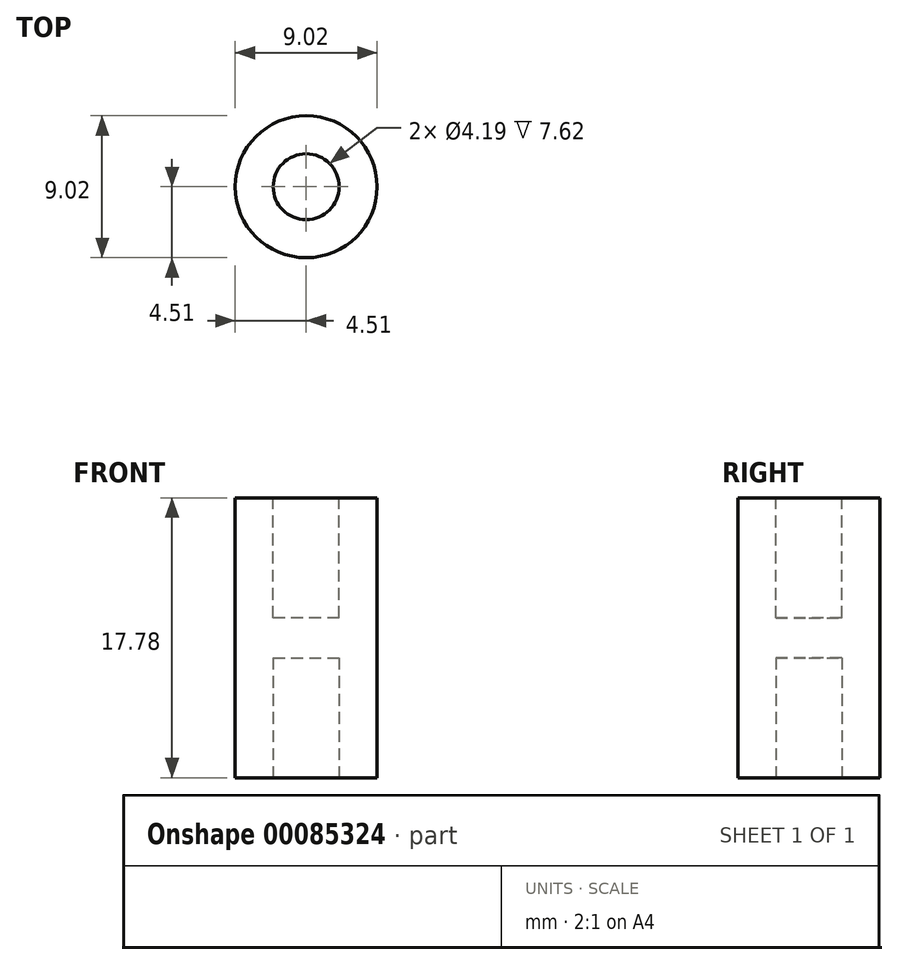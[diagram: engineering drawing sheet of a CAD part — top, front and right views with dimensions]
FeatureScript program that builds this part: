
annotation { "Feature Type Name" : "Feature", "Feature Type Description" : "" }
export const myFeature = defineFeature(function(context is Context, id is Id, definition is map)
    precondition{}
    {
        {
            var Q0;
            Q0=qCreatedBy(makeId("Top.planeOp"),FACE);
            var sketch = newSketch(context, id + "F0", { "sketchPlane" : qUnion([Q0])});
            skCircle(sketch, "E0", {"center": v(0, 0) * mm, "radius": 4.5 * mm});
            skSolve(sketch);
        }
        {
            var Q0;
            Q0 = qSketchRegion(id + "F0", true);
            extrude(context, id + "F1", {"entities" : qUnion([Q0]), "depth" : 17.78 * mm});
        }
        {
            var Q0;
            Q0=makeQuery(id+"F1.opExtrude","CAP_FACE",FACE,{"disambiguationData":[OSD([sQuery(id+"F0.wireOp",EDGE,"E0")])],"isStart":false});
            var sketch = newSketch(context, id + "F2", { "sketchPlane" : qUnion([Q0])});
            skCircle(sketch, "E1", {"center": v(0, 0) * mm, "radius": 2.1 * mm});
            skSolve(sketch);
        }
        {
            var Q0;
            Q0=makeQuery(id+"F2.imprint","IMPRINT",FACE,{"disambiguationData":[TD([[makeQuery(id+"F2.imprint","IMPRINT",EDGE,{"derivedFrom":sQuery(id+"F2.wireOp",EDGE,"E1")}),1.0]])]});
            extrude(context, id + "F3", {"entities" : qUnion([Q0]), "operationType" : NewBodyOperationType.REMOVE, "oppositeDirection" : true, "depth" : 7.62 * mm});
        }
        {
            var Q0;
            Q0=makeQuery(id+"F1.opExtrude","CAP_FACE",FACE,{"disambiguationData":[OSD([sQuery(id+"F0.wireOp",EDGE,"E0")])],"isStart":true});
            var sketch = newSketch(context, id + "F4", { "sketchPlane" : qUnion([Q0])});
            skCircle(sketch, "E2", {"center": v(0, 0) * mm, "radius": 2.1 * mm});
            skSolve(sketch);
        }
        {
            var Q0;
            Q0=makeQuery(id+"F4.imprint","IMPRINT",FACE,{"disambiguationData":[TD([[makeQuery(id+"F4.imprint","IMPRINT",EDGE,{"derivedFrom":sQuery(id+"F4.wireOp",EDGE,"E2")}),1.0]])]});
            extrude(context, id + "F5", {"entities" : qUnion([Q0]), "operationType" : NewBodyOperationType.REMOVE, "oppositeDirection" : true, "depth" : 7.62 * mm});
        }
    });
